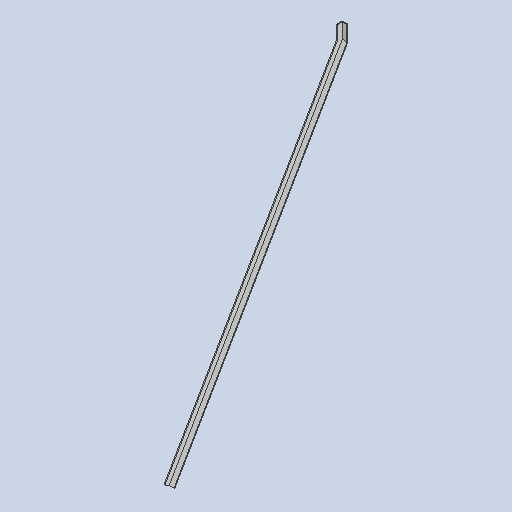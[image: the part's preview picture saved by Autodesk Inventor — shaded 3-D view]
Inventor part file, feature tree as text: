
AUTODESK INVENTOR PART (.ipt)
format: ipt  version: 2023 (Build 270158030, 158C)  size: 102,400 bytes
history: native  units: in
note: dims shown in document units (in); Inventor stores cm internally (conversion verified against a paired STEP export)
features: extrude x2, sketch x1
ambient origin geometry x8: Origin, YZ Plane, XZ Plane, XY Plane, X Axis, Y Axis, Z Axis, Center Point
bodies: Solid1 (feature_tree)
feature tree (3):
  sketch  "Sketch1"  dims[d0=45.0in d1=0.75in d2=45.0in d3=30.0deg d4=2.0in d5=0.75in d6=0.125in d7=45.0in d8=0.125in d9=0.125in d10=0.0in d11=0.625in d12=0.0in]
  extrude  "Extrusion1"  Depth=0.75in
  extrude  "Extrusion2"  Depth=45.0in
